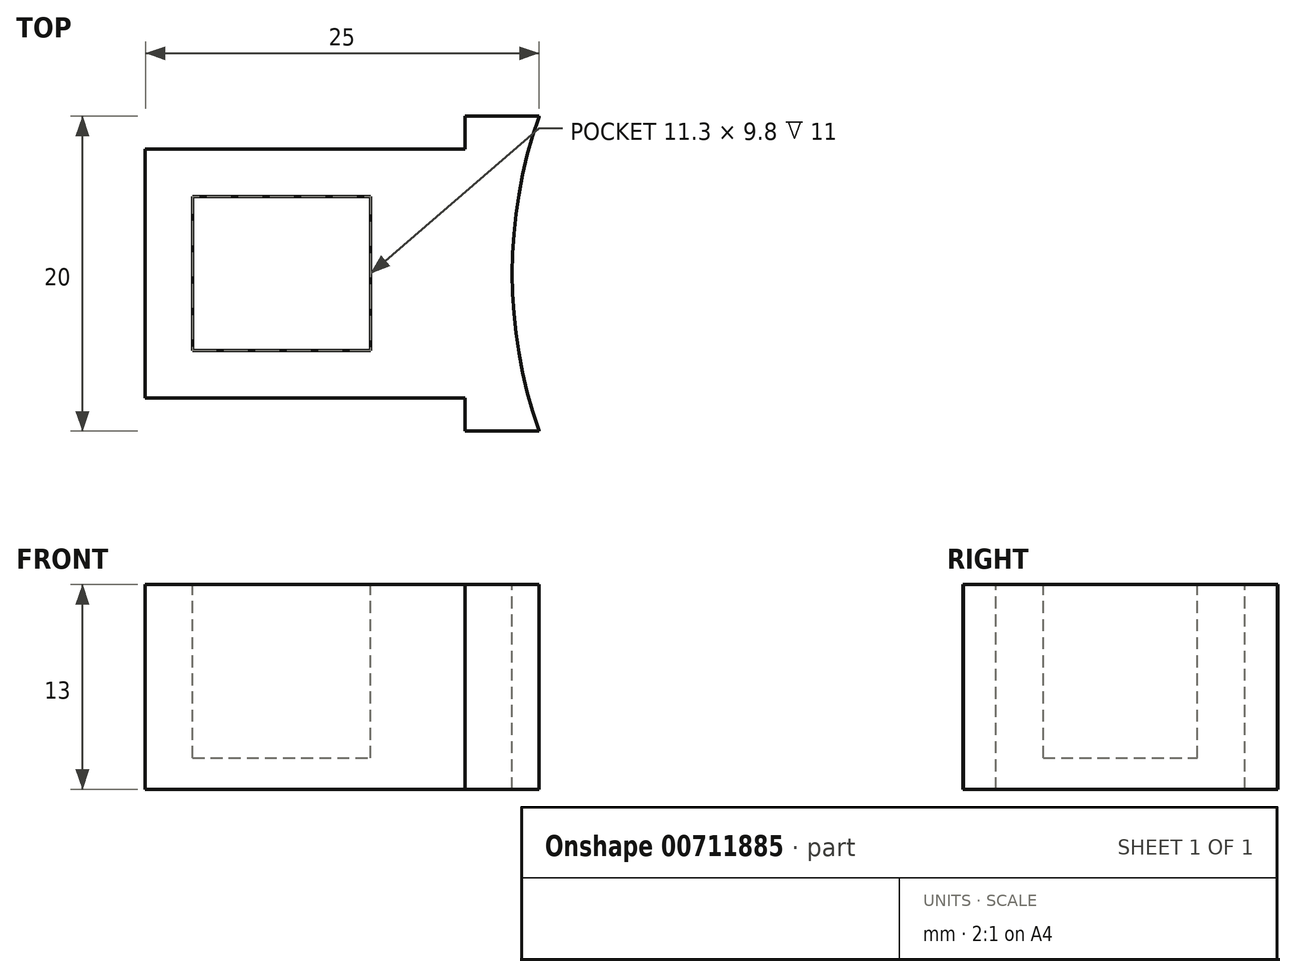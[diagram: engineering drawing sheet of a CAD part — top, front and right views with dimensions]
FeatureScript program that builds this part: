
annotation { "Feature Type Name" : "Feature", "Feature Type Description" : "" }
export const myFeature = defineFeature(function(context is Context, id is Id, definition is map)
    precondition{}
    {
        {
            var Q0;
            Q0=qCreatedBy(makeId("Top.planeOp"),FACE);
            var sketch = newSketch(context, id + "F0", { "sketchPlane" : qUnion([Q0])});
            skLineSegment(sketch, "E0.bottom", {"start": v(-42.97, 5.71) * mm, "end": v(-17.97, 5.71) * mm});
            skLineSegment(sketch, "E0.top", {"start": v(-42.97, -14.29) * mm, "end": v(-17.97, -14.29) * mm});
            skLineSegment(sketch, "E0.left", {"start": v(-42.97, 5.71) * mm, "end": v(-42.97, -14.29) * mm});
            skLineSegment(sketch, "E0.right", {"start": v(-17.97, 5.71) * mm, "end": v(-17.97, -14.29) * mm});
            skSolve(sketch);
        }
        {
            var Q0;
            Q0 = qSketchRegion(id + "F0", true);
            extrude(context, id + "F1", {"entities" : qUnion([Q0]), "depth" : 13 * mm, "offsetDistance" : 25 * mm});
        }
        {
            var Q0;
            Q0=makeQuery(id+"F1.opExtrude","CAP_FACE",FACE,{"disambiguationData":[OSD([sQuery(id+"F0.wireOp",EDGE,"E0.bottom"),sQuery(id+"F0.wireOp",EDGE,"E0.top"),sQuery(id+"F0.wireOp",EDGE,"E0.left"),sQuery(id+"F0.wireOp",EDGE,"E0.right")])],"isStart":false});
            var sketch = newSketch(context, id + "F2", { "sketchPlane" : qUnion([Q0])});
            skLineSegment(sketch, "E1.bottom", {"start": v(-39.97, -9.19) * mm, "end": v(-28.67, -9.19) * mm});
            skLineSegment(sketch, "E1.top", {"start": v(-39.97, 0.61) * mm, "end": v(-28.67, 0.61) * mm});
            skLineSegment(sketch, "E1.left", {"start": v(-39.97, -9.19) * mm, "end": v(-39.97, 0.61) * mm});
            skLineSegment(sketch, "E1.right", {"start": v(-28.67, -9.19) * mm, "end": v(-28.67, 0.61) * mm});
            skSolve(sketch);
        }
        {
            var Q0;
            Q0 = qSketchRegion(id + "F2", true);
            extrude(context, id + "F3", {"entities" : qUnion([Q0]), "operationType" : NewBodyOperationType.REMOVE, "oppositeDirection" : true, "depth" : 11 * mm, "offsetDistance" : 25 * mm});
        }
        {
            var Q0;
            Q0=makeQuery(id+"F1.opExtrude","CAP_FACE",FACE,{"disambiguationData":[OSD([sQuery(id+"F0.wireOp",EDGE,"E0.bottom"),sQuery(id+"F0.wireOp",EDGE,"E0.top"),sQuery(id+"F0.wireOp",EDGE,"E0.left"),sQuery(id+"F0.wireOp",EDGE,"E0.right")])],"isStart":false});
            var sketch = newSketch(context, id + "F4", { "sketchPlane" : qUnion([Q0])});
            skLineSegment(sketch, "E2.bottom", {"start": v(-42.97, 5.71) * mm, "end": v(-22.67, 5.71) * mm});
            skLineSegment(sketch, "E2.top", {"start": v(-42.97, 3.61) * mm, "end": v(-22.67, 3.61) * mm});
            skLineSegment(sketch, "E2.left", {"start": v(-42.97, 5.71) * mm, "end": v(-42.97, 3.61) * mm});
            skLineSegment(sketch, "E2.right", {"start": v(-22.67, 5.71) * mm, "end": v(-22.67, 3.61) * mm});
            skLineSegment(sketch, "E3.bottom", {"start": v(-42.97, -14.29) * mm, "end": v(-22.67, -14.29) * mm});
            skLineSegment(sketch, "E3.top", {"start": v(-42.97, -12.19) * mm, "end": v(-22.67, -12.19) * mm});
            skLineSegment(sketch, "E3.left", {"start": v(-42.97, -14.29) * mm, "end": v(-42.97, -12.19) * mm});
            skLineSegment(sketch, "E3.right", {"start": v(-22.67, -14.29) * mm, "end": v(-22.67, -12.19) * mm});
            skSolve(sketch);
        }
        {
            var Q0;
            Q0 = qSketchRegion(id + "F4", true);
            extrude(context, id + "F5", {"entities" : qUnion([Q0]), "operationType" : NewBodyOperationType.REMOVE, "oppositeDirection" : true, "depth" : 25 * mm, "offsetDistance" : 25 * mm});
        }
        {
            var Q0;
            Q0=makeQuery(id+"F1.opExtrude","CAP_FACE",FACE,{"disambiguationData":[OSD([sQuery(id+"F0.wireOp",EDGE,"E0.bottom"),sQuery(id+"F0.wireOp",EDGE,"E0.top"),sQuery(id+"F0.wireOp",EDGE,"E0.left"),sQuery(id+"F0.wireOp",EDGE,"E0.right")])],"isStart":false});
            var sketch = newSketch(context, id + "F6", { "sketchPlane" : qUnion([Q0])});
            skCircle(sketch, "E4", {"center": v(10.33, -4.29) * mm, "radius": 30 * mm});
            skSolve(sketch);
        }
        {
            var Q0;
            Q0 = qSketchRegion(id + "F6", true);
            extrude(context, id + "F7", {"entities" : qUnion([Q0]), "operationType" : NewBodyOperationType.REMOVE, "oppositeDirection" : true, "depth" : 25 * mm, "offsetDistance" : 25 * mm});
        }
    });
